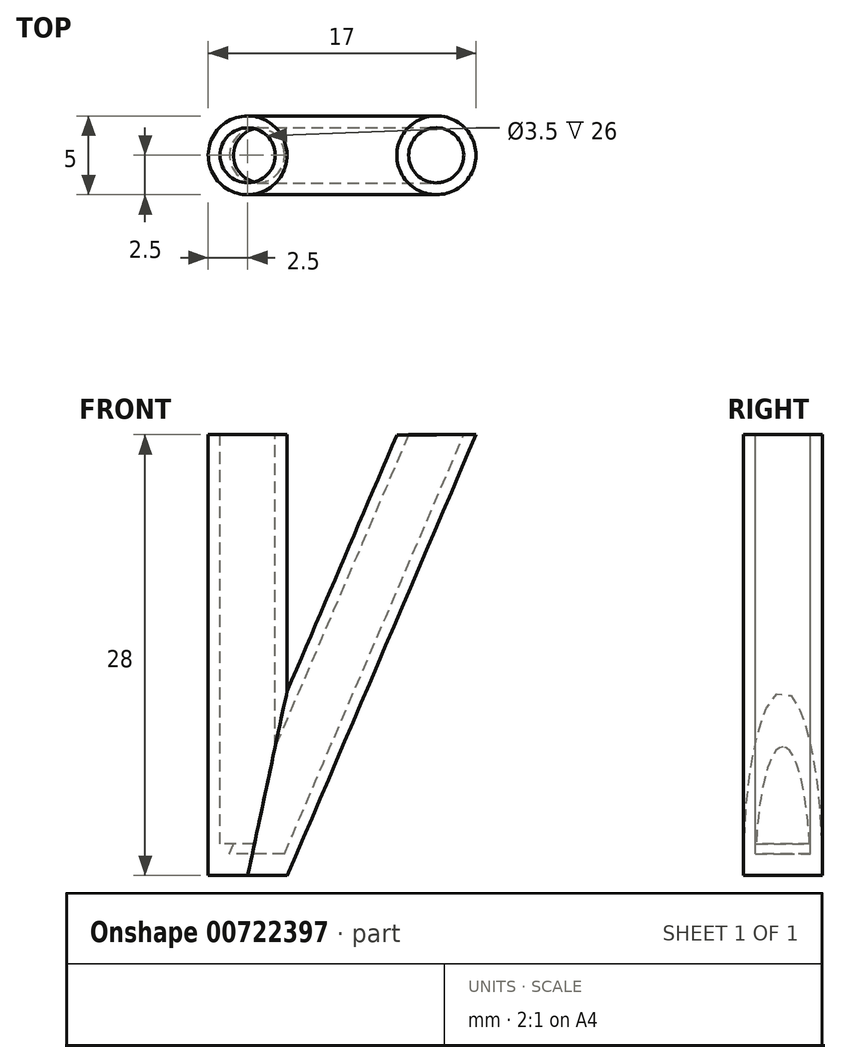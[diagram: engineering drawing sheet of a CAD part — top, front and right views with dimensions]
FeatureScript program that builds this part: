
annotation { "Feature Type Name" : "Feature", "Feature Type Description" : "" }
export const myFeature = defineFeature(function(context is Context, id is Id, definition is map)
    precondition{}
    {
        {
            var Q0;
            Q0=qCreatedBy(makeId("Top.planeOp"),FACE);
            var sketch = newSketch(context, id + "F0", { "sketchPlane" : qUnion([Q0])});
            skCircle(sketch, "E0", {"center": v(0, 0) * mm, "radius": 2.5 * mm});
            skSolve(sketch);
        }
        {
            var Q0;
            Q0=makeQuery(id+"F0.imprint","IMPRINT",FACE,{"disambiguationData":[TD([[makeQuery(id+"F0.imprint","IMPRINT",EDGE,{"derivedFrom":sQuery(id+"F0.wireOp",EDGE,"E0")}),1.0]])]});
            extrude(context, id + "F1", {"entities" : qUnion([Q0]), "depth" : 28 * mm, "offsetDistance" : 25 * mm});
        }
        {
            var Q0;
            Q0=makeQuery(id+"F1.opExtrude","CAP_FACE",FACE,{"disambiguationData":[OSD([sQuery(id+"F0.wireOp",EDGE,"E0")])],"isStart":false});
            var sketch = newSketch(context, id + "F2", { "sketchPlane" : qUnion([Q0])});
            skCircle(sketch, "E1", {"center": v(0, 0) * mm, "radius": 1.75 * mm});
            skSolve(sketch);
        }
        {
            var Q0;
            Q0=makeQuery(id+"F2.imprint","IMPRINT",FACE,{"disambiguationData":[TD([[makeQuery(id+"F2.imprint","IMPRINT",EDGE,{"derivedFrom":sQuery(id+"F2.wireOp",EDGE,"E1")}),1.0]])]});
            var sketch = newSketch(context, id + "F3", { "sketchPlane" : qUnion([Q0])});
            skCircle(sketch, "E2", {"center": v(12, 0) * mm, "radius": 2.5 * mm});
            skSolve(sketch);
        }
        {
            var Q0;
            Q0=qCreatedBy(makeId("Front.planeOp"),FACE);
            var sketch = newSketch(context, id + "F4", { "sketchPlane" : qUnion([Q0])});
            skLineSegment(sketch, "E3", {"start": v(0, 0) * mm, "end": v(11.98, 28) * mm});
            skLineSegment(sketch, "E4", {"start": v(11.98, 28) * mm, "end": v(0.6, 1.38) * mm});
            skSolve(sketch);
        }
        {
            var Q0;
            Q0=makeQuery(id+"F3.imprint","IMPRINT",FACE,{"disambiguationData":[TD([[makeQuery(id+"F3.imprint","IMPRINT",EDGE,{"derivedFrom":sQuery(id+"F3.wireOp",EDGE,"E2")}),1.0]])]});
            var Q1;
            Q1=makeQuery(id+"F1.opExtrude","CAP_FACE",FACE,{"disambiguationData":[OSD([sQuery(id+"F0.wireOp",EDGE,"E0")])],"isStart":true});
            var Q2;
            Q2=sQuery(id+"F4.wireOp",EDGE,"E3");
            sweep(context, id + "F5", {"operationType" : NewBodyOperationType.ADD, "profiles" : qUnion([Q0, Q1]), "path" : qUnion([Q2])});
        }
        {
            var Q0;
            Q0=makeQuery(id+"F3.imprint","IMPRINT",FACE,{"disambiguationData":[TD([[makeQuery(id+"F3.imprint","IMPRINT",EDGE,{"derivedFrom":makeQuery(id+"F2.imprint","IMPRINT",EDGE,{"derivedFrom":sQuery(id+"F2.wireOp",EDGE,"E1")})}),1.0]])]});
            extrude(context, id + "F6", {"entities" : qUnion([Q0]), "operationType" : NewBodyOperationType.REMOVE, "oppositeDirection" : true, "depth" : 26 * mm, "offsetDistance" : 25 * mm});
        }
        {
            var Q0;
            Q0=makeQuery(id+"F3.imprint","IMPRINT",FACE,{"disambiguationData":[TD([[makeQuery(id+"F3.imprint","IMPRINT",EDGE,{"derivedFrom":sQuery(id+"F3.wireOp",EDGE,"E2")}),1.0]])]});
            var sketch = newSketch(context, id + "F7", { "sketchPlane" : qUnion([Q0])});
            skCircle(sketch, "E5", {"center": v(11.98, 0) * mm, "radius": 1.75 * mm});
            skSolve(sketch);
        }
        {
            var Q0;
            Q0=makeQuery(id+"F7.imprint","IMPRINT",FACE,{"disambiguationData":[TD([[makeQuery(id+"F7.imprint","IMPRINT",EDGE,{"derivedFrom":sQuery(id+"F7.wireOp",EDGE,"E5")}),1.0]])]});
            var Q1;
            Q1=sQuery(id+"F7.wireOp",EDGE,"E5");
            var Q2;
            Q2=sQuery(id+"F4.wireOp",EDGE,"E4");
            sweep(context, id + "F8", {"operationType" : NewBodyOperationType.REMOVE, "profiles" : qUnion([Q0]), "surfaceProfiles" : qUnion([Q1]), "path" : qUnion([Q2])});
        }
    });
